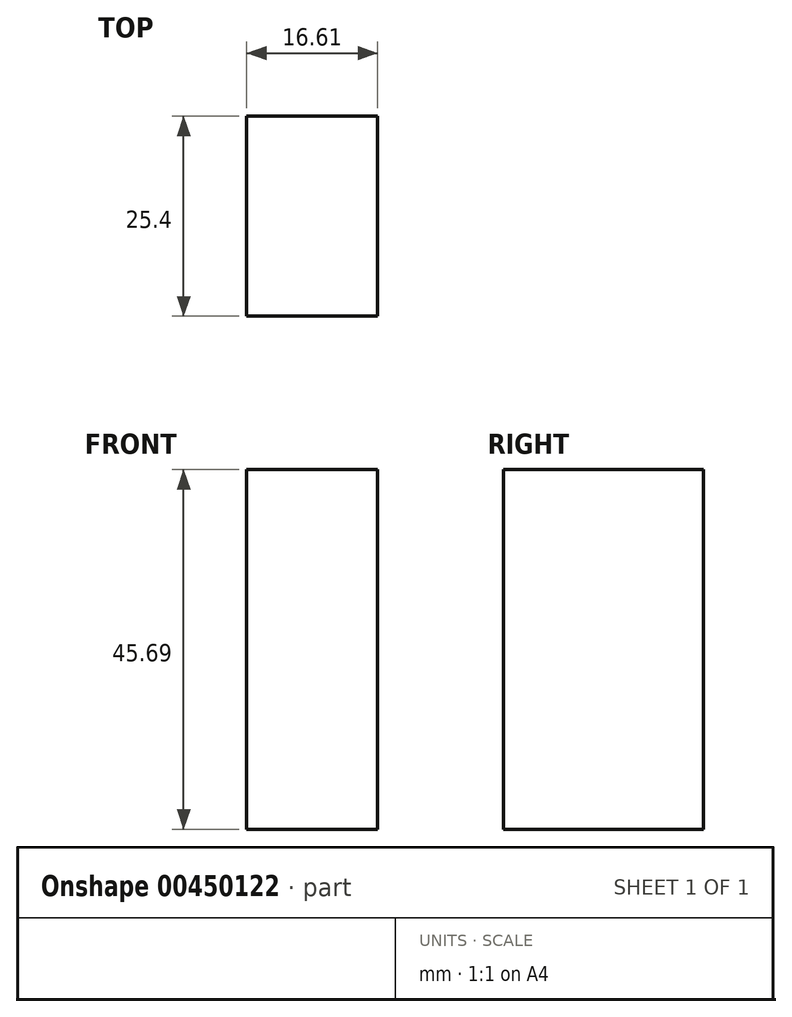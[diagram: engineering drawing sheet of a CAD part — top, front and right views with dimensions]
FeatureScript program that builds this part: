
annotation { "Feature Type Name" : "Feature", "Feature Type Description" : "" }
export const myFeature = defineFeature(function(context is Context, id is Id, definition is map)
    precondition{}
    {
        {
            var Q0;
            Q0=qCreatedBy(makeId("Front.planeOp"),FACE);
            var sketch = newSketch(context, id + "F0", { "sketchPlane" : qUnion([Q0])});
            skLineSegment(sketch, "E0.bottom", {"start": v(16.6, 45.69) * mm, "end": v(0, 45.69) * mm});
            skLineSegment(sketch, "E0.top", {"start": v(16.6, 0) * mm, "end": v(0, 0) * mm});
            skLineSegment(sketch, "E0.left", {"start": v(16.6, 45.69) * mm, "end": v(16.6, 0) * mm});
            skLineSegment(sketch, "E0.right", {"start": v(0, 45.69) * mm, "end": v(0, 0) * mm});
            skSolve(sketch);
        }
        {
            var Q0;
            Q0=makeQuery(id+"F0.imprint","IMPRINT",FACE,{"disambiguationData":[TD([[makeQuery(id+"F0.imprint","IMPRINT",EDGE,{"derivedFrom":sQuery(id+"F0.wireOp",EDGE,"E0.bottom")}),1.0]])]});
            extrude(context, id + "F1", {"entities" : qUnion([Q0]), "depth" : 25.4 * mm});
        }
    });
